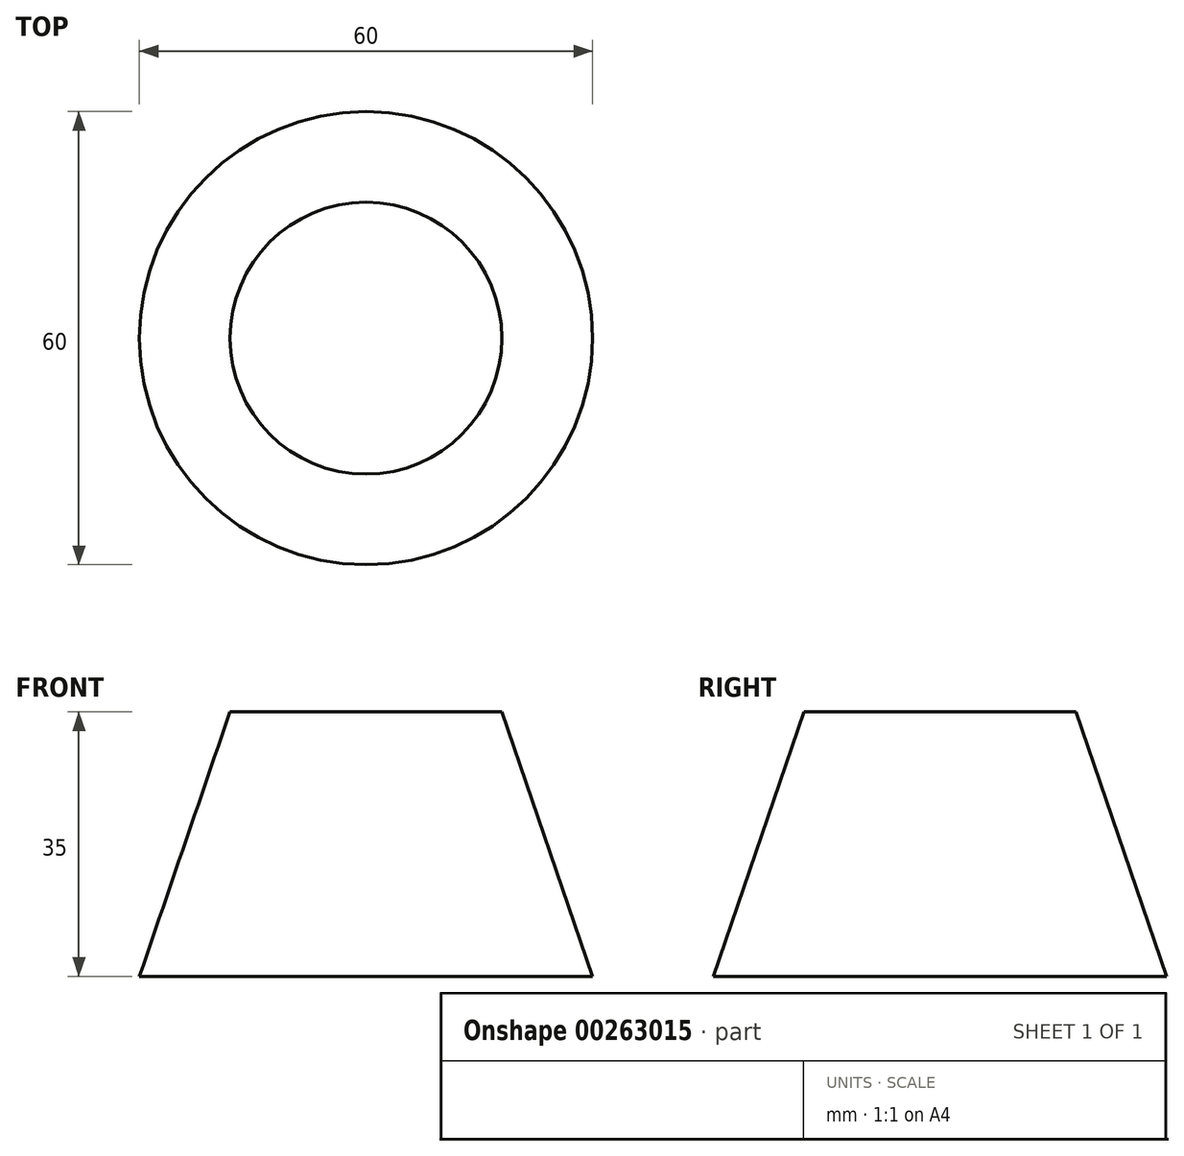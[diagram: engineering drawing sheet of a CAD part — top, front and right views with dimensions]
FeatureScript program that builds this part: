
annotation { "Feature Type Name" : "Feature", "Feature Type Description" : "" }
export const myFeature = defineFeature(function(context is Context, id is Id, definition is map)
    precondition{}
    {
        {
            var Q0;
            Q0=qCreatedBy(makeId("Front.planeOp"),FACE);
            var sketch = newSketch(context, id + "F0", { "sketchPlane" : qUnion([Q0])});
            skLineSegment(sketch, "E0", {"start": v(0, 0) * mm, "end": v(0, 35) * mm});
            skLineSegment(sketch, "E1", {"start": v(0, 35) * mm, "end": v(18, 35) * mm});
            skLineSegment(sketch, "E2", {"start": v(18, 35) * mm, "end": v(30, 0) * mm});
            skLineSegment(sketch, "E3", {"start": v(0, 0) * mm, "end": v(30, 0) * mm});
            skLineSegment(sketch, "E4", {"start": v(0, 63.17) * mm, "end": v(0, -48.98) * mm, "construction": true});
            skSolve(sketch);
        }
        {
            var Q0;
            Q0=makeQuery(id+"F0.imprint","IMPRINT",FACE,{"disambiguationData":[TD([[makeQuery(id+"F0.imprint","IMPRINT",EDGE,{"derivedFrom":sQuery(id+"F0.wireOp",EDGE,"E0")}),-1.0]])]});
            var Q1;
            Q1=sQuery(id+"F0.wireOp",EDGE,"E4");
            revolve(context, id + "F1", {"entities" : qUnion([Q0]), "axis" : qUnion([Q1]), "revolveType" : RevolveType.FULL, "oppositeDirection" : true});
        }
    });
